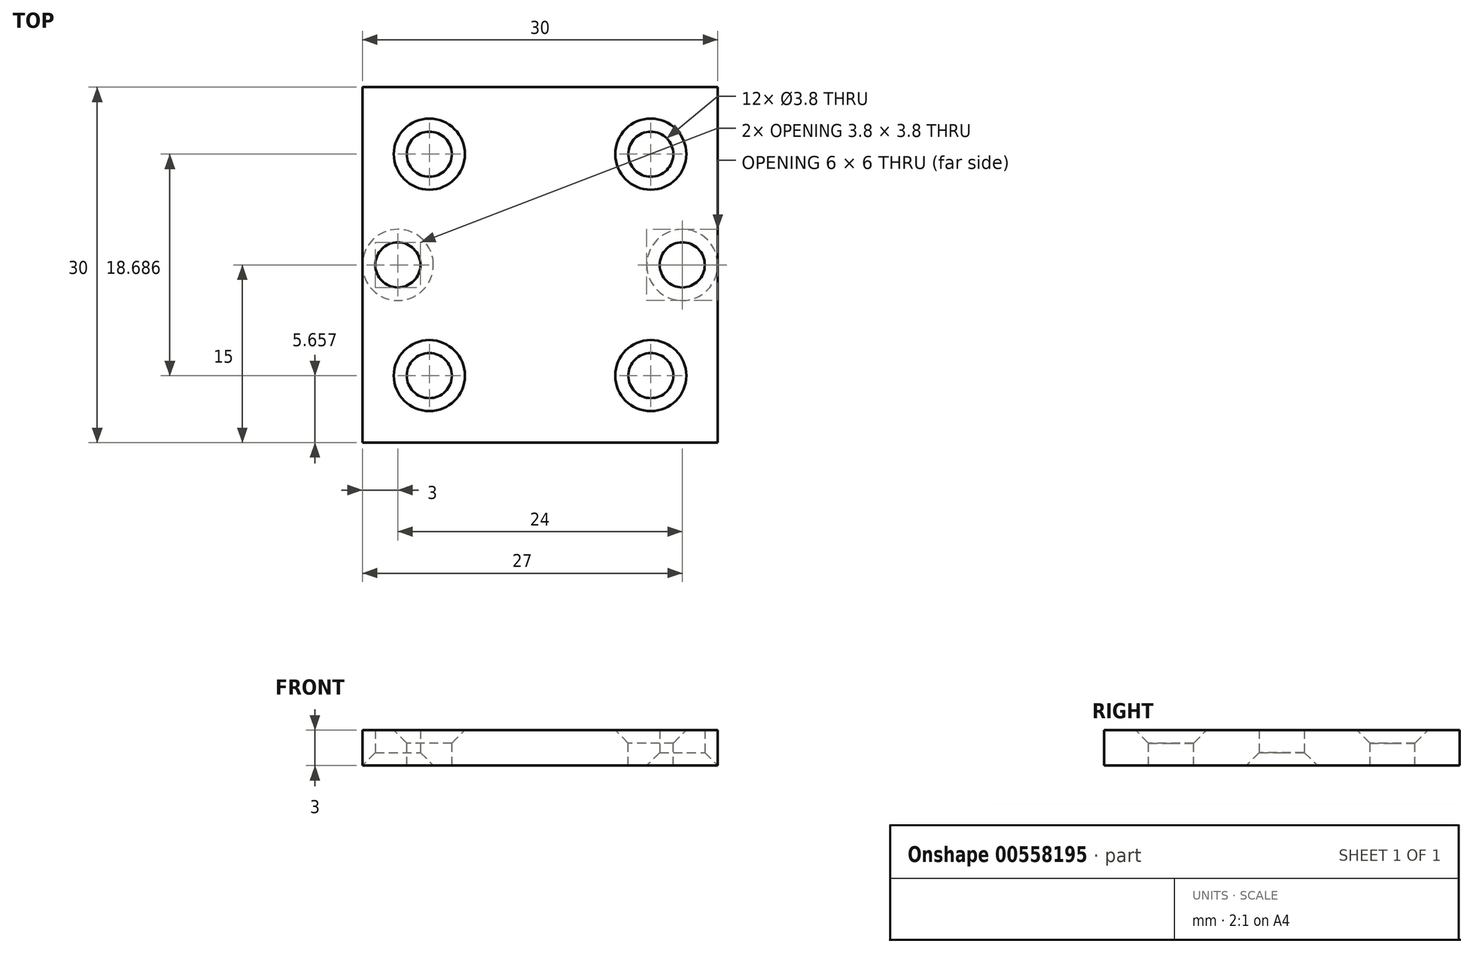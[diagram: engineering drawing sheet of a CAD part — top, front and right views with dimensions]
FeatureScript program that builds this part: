
annotation { "Feature Type Name" : "Feature", "Feature Type Description" : "" }
export const myFeature = defineFeature(function(context is Context, id is Id, definition is map)
    precondition{}
    {
        {
            var Q0;
            Q0=qCreatedBy(makeId("Top.planeOp"),FACE);
            var sketch = newSketch(context, id + "F0", { "sketchPlane" : qUnion([Q0])});
            skLineSegment(sketch, "E0.bottom", {"start": v(15, 15) * mm, "end": v(-15, 15) * mm});
            skLineSegment(sketch, "E0.top", {"start": v(15, -15) * mm, "end": v(-15, -15) * mm});
            skLineSegment(sketch, "E0.left", {"start": v(15, 15) * mm, "end": v(15, -15) * mm});
            skLineSegment(sketch, "E0.right", {"start": v(-15, 15) * mm, "end": v(-15, -15) * mm});
            skPoint(sketch, "E0.middle", {"position": v(0, 0) * mm});
            skLineSegment(sketch, "E1", {"start": v(-15, 15) * mm, "end": v(15, -15) * mm});
            skPoint(sketch, "E2", {"position": v(-9.34, 9.34) * mm});
            skPoint(sketch, "E3", {"position": v(9.34, -9.34) * mm});
            skLineSegment(sketch, "E4", {"start": v(15, 15) * mm, "end": v(-15, -15) * mm});
            skPoint(sketch, "E5", {"position": v(9.34, 9.34) * mm});
            skPoint(sketch, "E6", {"position": v(-9.34, -9.34) * mm});
            skPoint(sketch, "E7", {"position": v(12, 0) * mm});
            skPoint(sketch, "E7.positionSnap0", {"position": v(15, 0) * mm});
            skPoint(sketch, "E8.MirrorP", {"position": v(-12, 0) * mm});
            skSolve(sketch);
        }
        {
            var Q0;
            Q0 = qSketchRegion(id + "F0", true);
            extrude(context, id + "F1", {"entities" : qUnion([Q0]), "oppositeDirection" : true, "depth" : 3 * mm, "offsetDistance" : 25 * mm});
        }
        {
            var Q0;
            Q0=sQuery(id+"F0.wireOp",VERTEX,"E2");
            var Q1;
            Q1=sQuery(id+"F0.wireOp",VERTEX,"E5");
            var Q2;
            Q2=sQuery(id+"F0.wireOp",VERTEX,"E6");
            var Q3;
            Q3=sQuery(id+"F0.wireOp",VERTEX,"E3");
            var Q4;
            Q4=makeQuery(id+"F1.opExtrude","SWEPT_BODY",BODY,{"disambiguationData":[OSD([sQuery(id+"F0.wireOp",EDGE,"E0.bottom"),sQuery(id+"F0.wireOp",EDGE,"E0.top"),sQuery(id+"F0.wireOp",EDGE,"E0.left"),sQuery(id+"F0.wireOp",EDGE,"E0.right")])]});
            hole(context, id + "F2", {"style" : HoleStyle.C_SINK, "endStyle" : HoleEndStyle.THROUGH, "holeDiameter" : 3.8 * mm, "cSinkDiameter" : 6 * mm, "cSinkAngle" : 90 * degree, "isTappedThrough" : true, "tappedDepth" : 12 * mm, "tapClearance" : 3, "locations" : qUnion([Q0, Q1, Q2, Q3]), "scope" : qUnion([Q4])});
        }
        {
            var Q0;
            Q0=makeQuery(id+"F1.opExtrude","CAP_FACE",FACE,{"disambiguationData":[OSD([sQuery(id+"F0.wireOp",EDGE,"E0.bottom"),sQuery(id+"F0.wireOp",EDGE,"E0.top"),sQuery(id+"F0.wireOp",EDGE,"E0.left"),sQuery(id+"F0.wireOp",EDGE,"E0.right")])],"isStart":false});
            var sketch = newSketch(context, id + "F3", { "sketchPlane" : qUnion([Q0])});
            skPoint(sketch, "E9", {"position": v(-12, 0) * mm});
            skPoint(sketch, "E10.MirrorP", {"position": v(12, 0) * mm});
            skSolve(sketch);
        }
        {
            var Q0;
            Q0=sQuery(id+"F3.wireOp",VERTEX,"E9");
            var Q1;
            Q1=sQuery(id+"F3.wireOp",VERTEX,"E10.MirrorP");
            var Q2;
            Q2=makeQuery(id+"F1.opExtrude","SWEPT_BODY",BODY,{"disambiguationData":[OSD([sQuery(id+"F0.wireOp",EDGE,"E0.bottom"),sQuery(id+"F0.wireOp",EDGE,"E0.top"),sQuery(id+"F0.wireOp",EDGE,"E0.left"),sQuery(id+"F0.wireOp",EDGE,"E0.right")])]});
            hole(context, id + "F4", {"style" : HoleStyle.C_SINK, "endStyle" : HoleEndStyle.THROUGH, "holeDiameter" : 3.8 * mm, "cSinkDiameter" : 6 * mm, "cSinkAngle" : 90 * degree, "isTappedThrough" : true, "tappedDepth" : 12 * mm, "tapClearance" : 3, "locations" : qUnion([Q0, Q1]), "scope" : qUnion([Q2])});
        }
    });
